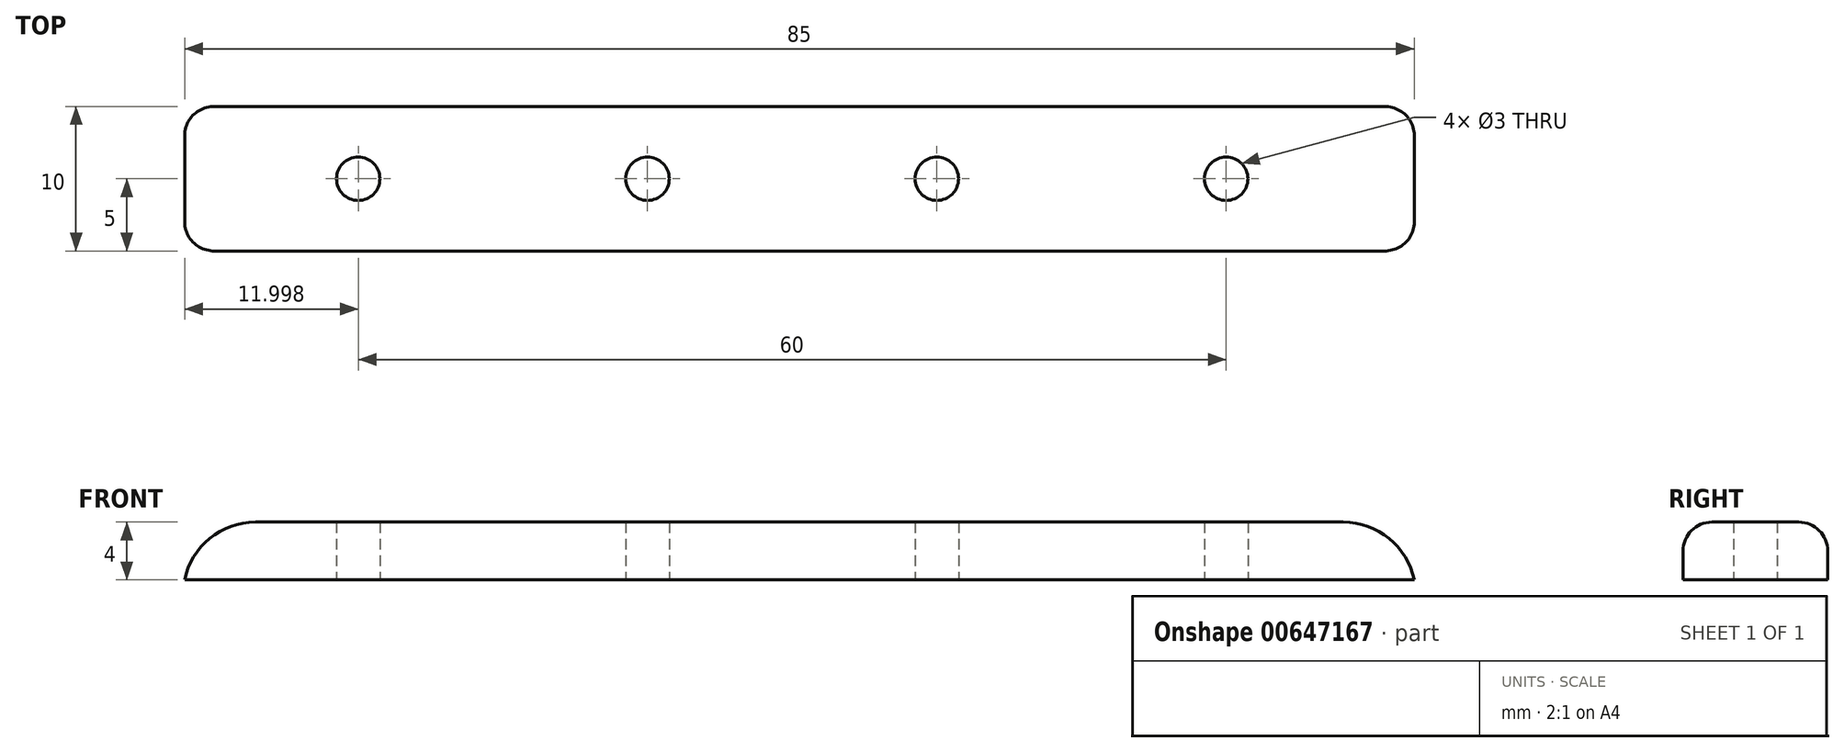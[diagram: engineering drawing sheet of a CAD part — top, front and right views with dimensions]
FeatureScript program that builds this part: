
annotation { "Feature Type Name" : "Feature", "Feature Type Description" : "" }
export const myFeature = defineFeature(function(context is Context, id is Id, definition is map)
    precondition{}
    {
        {
            var Q0;
            Q0=qCreatedBy(makeId("Top.planeOp"),FACE);
            var sketch = newSketch(context, id + "F0", { "sketchPlane" : qUnion([Q0])});
            skCircle(sketch, "E0", {"center": v(-24.64, 5) * mm, "radius": 1.5 * mm});
            skLineSegment(sketch, "E1", {"start": v(-24.64, 7.97) * mm, "end": v(-24.64, 2.03) * mm});
            skCircle(sketch, "E2", {"center": v(-4.64, 5) * mm, "radius": 1.5 * mm});
            skCircle(sketch, "E3", {"center": v(15.36, 5) * mm, "radius": 1.5 * mm});
            skCircle(sketch, "E4", {"center": v(35.36, 5) * mm, "radius": 1.5 * mm});
            skLineSegment(sketch, "E5.bottom", {"start": v(-36.64, 10) * mm, "end": v(48.36, 10) * mm});
            skLineSegment(sketch, "E5.top", {"start": v(-36.64, 0) * mm, "end": v(48.36, 0) * mm});
            skLineSegment(sketch, "E5.left", {"start": v(-36.64, 10) * mm, "end": v(-36.64, 0) * mm});
            skLineSegment(sketch, "E5.right", {"start": v(48.36, 10) * mm, "end": v(48.36, 0) * mm});
            skSolve(sketch);
        }
        {
            var Q0;
            Q0=makeQuery(id+"F0.imprint","IMPRINT",FACE,{"disambiguationData":[TD([[makeQuery(id+"F0.imprint","IMPRINT",EDGE,{"derivedFrom":sQuery(id+"F0.wireOp",EDGE,"E2")}),-1.0]])]});
            extrude(context, id + "F1", {"entities" : qUnion([Q0]), "depth" : 4 * mm, "offsetDistance" : 25 * mm});
        }
        {
            var Q0;
            Q0=makeQuery(id+"F1.opExtrude","CAP_EDGE",EDGE,{"disambiguationData":[OSD([sQuery(id+"F0.wireOp",EDGE,"E5.left")])],"isStart":false});
            var Q1;
            Q1=makeQuery(id+"F1.opExtrude","CAP_EDGE",EDGE,{"disambiguationData":[OSD([sQuery(id+"F0.wireOp",EDGE,"E5.right")])],"isStart":false});
            fillet(context, id + "F2", {"entities" : qUnion([Q0, Q1]), "radius" : 5 * mm, "tangentPropagation" : true, "allowEdgeOverflow" : false});
        }
        {
            var Q0;
            Q0=makeQuery(id+"F1.opExtrude","CAP_EDGE",EDGE,{"disambiguationData":[OSD([sQuery(id+"F0.wireOp",EDGE,"E5.bottom")])],"isStart":false});
            var Q1;
            Q1=makeQuery(id+"F1.opExtrude","CAP_EDGE",EDGE,{"disambiguationData":[OSD([sQuery(id+"F0.wireOp",EDGE,"E5.top")])],"isStart":false});
            fillet(context, id + "F3", {"entities" : qUnion([Q0, Q1]), "radius" : 2 * mm, "tangentPropagation" : true, "allowEdgeOverflow" : false});
        }
    });
